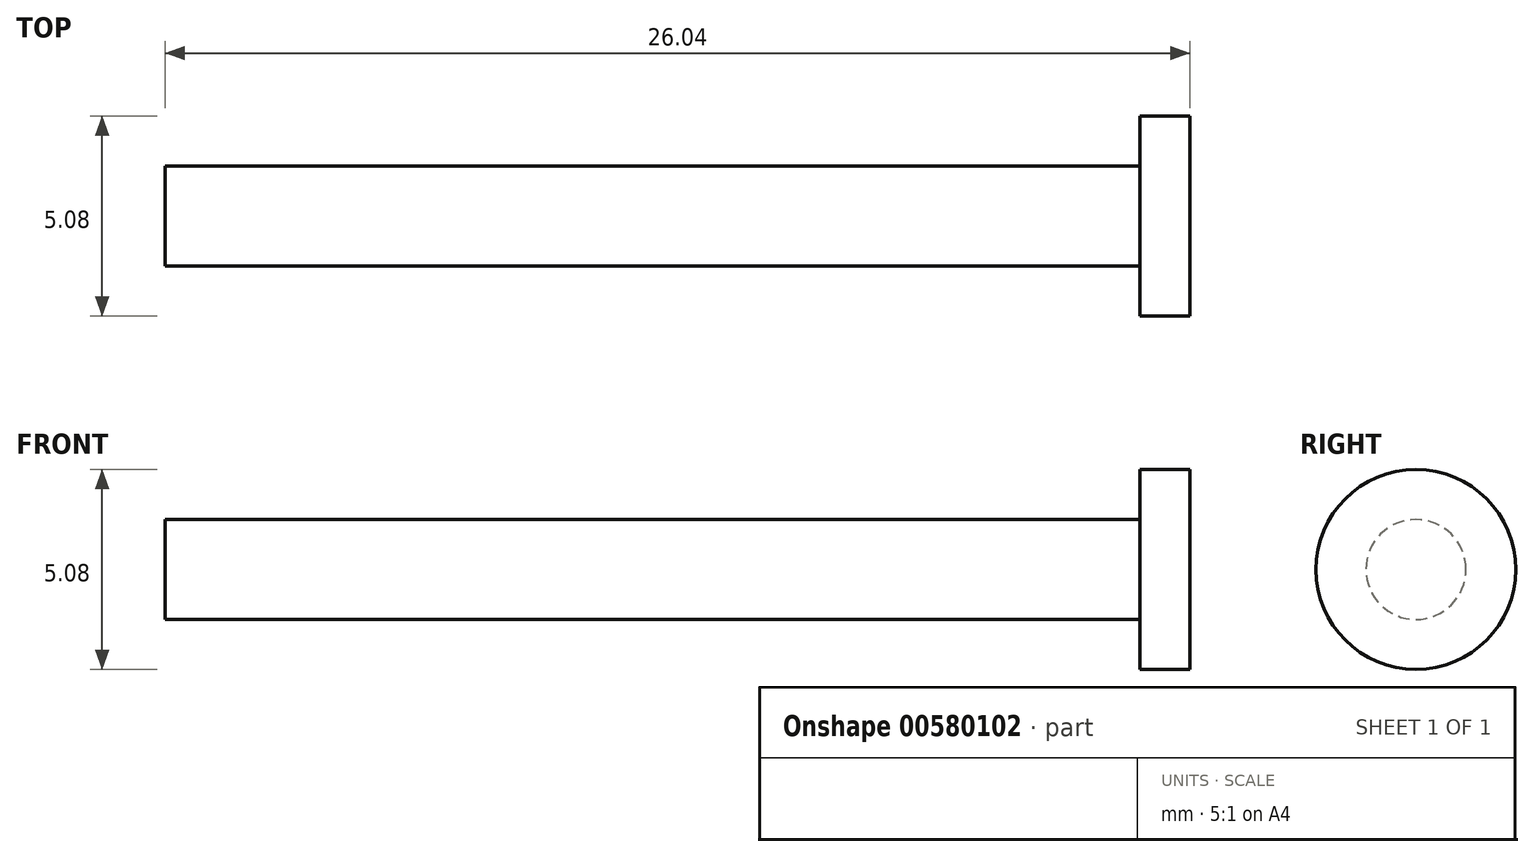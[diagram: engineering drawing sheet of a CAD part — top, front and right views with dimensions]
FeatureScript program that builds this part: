
annotation { "Feature Type Name" : "Feature", "Feature Type Description" : "" }
export const myFeature = defineFeature(function(context is Context, id is Id, definition is map)
    precondition{}
    {
        {
            var Q0;
            Q0=qCreatedBy(makeId("Right.planeOp"),FACE);
            var sketch = newSketch(context, id + "F0", { "sketchPlane" : qUnion([Q0])});
            skCircle(sketch, "E0", {"center": v(0, 0) * mm, "radius": 1.27 * mm});
            skSolve(sketch);
        }
        {
            var Q0;
            Q0=qSketchRegion(id+"F0",true);
            extrude(context, id + "F1", {"entities" : qUnion([Q0]), "depth" : 25.4 * mm});
        }
        {
            var Q0;
            Q0=makeQuery(id+"F1.opExtrude","CAP_FACE",FACE,{"disambiguationData":[OSD([sQuery(id+"F0.wireOp",EDGE,"E0")])],"isStart":false});
            var sketch = newSketch(context, id + "F2", { "sketchPlane" : qUnion([Q0])});
            skCircle(sketch, "E1", {"center": v(0, 0) * mm, "radius": 2.54 * mm});
            skSolve(sketch);
        }
        {
            var Q0;
            Q0=qSketchRegion(id+"F2",true);
            extrude(context, id + "F3", {"entities" : qUnion([Q0]), "operationType" : NewBodyOperationType.ADD, "depth" : 1.27 * mm, "symmetric" : true});
        }
    });
